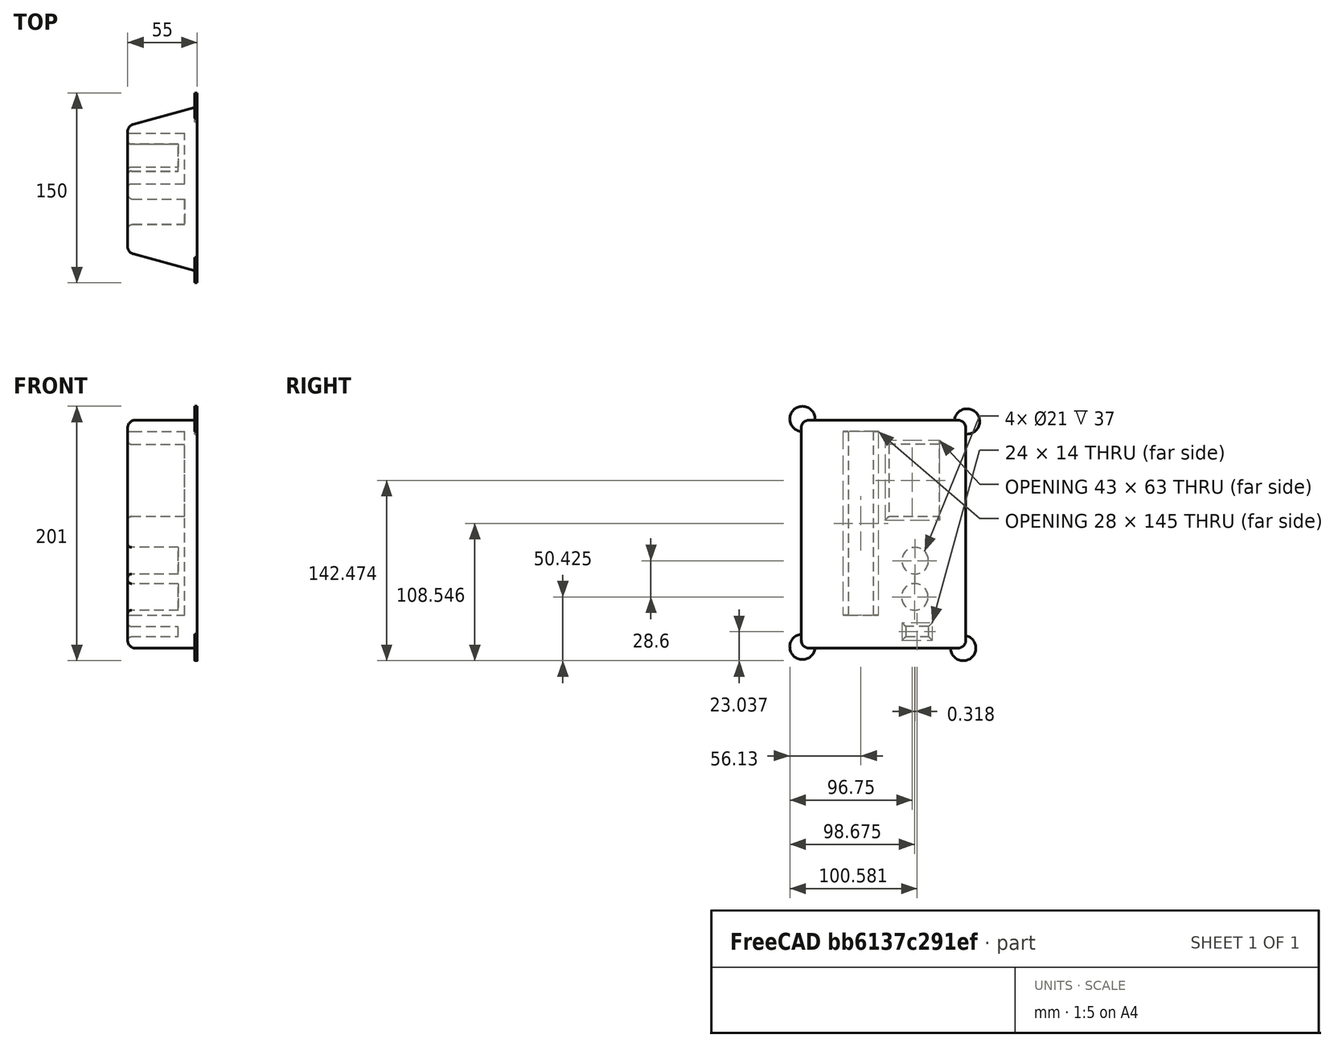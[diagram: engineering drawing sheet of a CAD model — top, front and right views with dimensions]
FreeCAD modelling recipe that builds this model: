
FCSTD DOCUMENT  (FreeCAD 0.19R)
Label: KeyboardTray
License: All rights reserved
LicenseURL: http://en.wikipedia.org/wiki/All_rights_reserved
objects: PartDesign::Fillet×5, Sketcher::SketchObject×4, Part::Cylinder×4, PartDesign::Pocket×3, PartDesign::Pad×1, PartDesign::Body×1, Part::MultiFuse×1, Mesh::Feature×1
note: 28 computed .brp shape members not serialized (recipe doc carries the construction recipe); baked Part::Feature solids carry a one-line shape summary decoded from their .brp

FEATURE [Sketcher::SketchObject] Sketch
  FullyConstrained = true
  MapMode = 5
  Support = -> [XY_Plane]
  sketch-geometry (4):
    g0: LineSegment StartX=-55 StartY=50 StartZ=0 EndX=0 EndY=65 EndZ=0
    g1: LineSegment StartX=0 StartY=65 StartZ=0 EndX=0 EndY=-65 EndZ=0
    g2: LineSegment StartX=0 StartY=-65 StartZ=0 EndX=-55 EndY=-50 EndZ=0
    g3: LineSegment StartX=-55 StartY=-50 StartZ=0 EndX=-55 EndY=50 EndZ=0
  constraints (10):
    c: Coincident(g0,g1)
    c: Coincident(g1,g2)
    c: Coincident(g2,g3)
    c: Coincident(g3,g0)
    c: Distance(g1) = 130
    c: Distance(g3) = 100
    c: DistanceX(g0,g0) = 55
    c: PointOnObject(g1,g-2)
    c: Symmetric(g1,g0,g-1)
    c: Symmetric(g2,g0,g-1)
FEATURE [PartDesign::Pad] Pad
  Direction = (1,1,1)
  Length = 180
  Length2 = 100
  Midplane = true
  Profile = -> Sketch
  Type = 0
FEATURE [Sketcher::SketchObject] Sketch001
  FullyConstrained = false
  MapMode = 5
  Placement = pos=(-55,0,0) rot=(0.57735,-0.57735,-0.57735;2.0944rad)
  Support = -> [Pad]
  sketch-geometry (4):
    g0: LineSegment StartX=7.87036 StartY=81.0461 StartZ=0 EndX=27.8704 EndY=81.0461 EndZ=0
    g1: LineSegment StartX=27.8704 StartY=81.0461 StartZ=0 EndX=27.7064 EndY=-63.9538 EndZ=0
    g2: LineSegment StartX=27.7064 StartY=-63.9538 StartZ=0 EndX=7.87036 EndY=-63.9538 EndZ=0
    g3: LineSegment StartX=7.87036 StartY=-63.9538 StartZ=0 EndX=7.87036 EndY=81.0461 EndZ=0
  constraints (9):
    c: Coincident(g0,g1)
    c: Coincident(g1,g2)
    c: Coincident(g2,g3)
    c: Coincident(g3,g0)
    c: Horizontal(g2)
    c: Vertical(g3)
    c: Distance(g1) = 145
    c: Distance(g0) = 20
    c: Perpendicular(g0,g3)
FEATURE [PartDesign::Pocket] Pocket
  BaseFeature = -> Pad
  Length = 45
  Length2 = 100
  Profile = -> Sketch001
  Type = 0
FEATURE [Sketcher::SketchObject] Sketch002
  FullyConstrained = false
  MapMode = 5
  Placement = pos=(-55,0,0) rot=(0.57735,-0.57735,-0.57735;2.0944rad)
  Support = -> [Pocket]
  sketch-geometry (4):
    g0: LineSegment StartX=-44.2497 StartY=70.9741 StartZ=0 EndX=-4.24974 EndY=70.9741 EndZ=0
    g1: LineSegment StartX=-4.24974 StartY=70.9741 StartZ=0 EndX=-4.24974 EndY=13.9741 EndZ=0
    g2: LineSegment StartX=-4.24974 StartY=13.9741 StartZ=0 EndX=-44.2497 EndY=13.9741 EndZ=0
    g3: LineSegment StartX=-44.2497 StartY=13.9741 StartZ=0 EndX=-44.2497 EndY=70.9741 EndZ=0
  constraints (10):
    c: Coincident(g0,g1)
    c: Coincident(g1,g2)
    c: Coincident(g2,g3)
    c: Coincident(g3,g0)
    c: Horizontal(g0)
    c: Horizontal(g2)
    c: Vertical(g1)
    c: Vertical(g3)
    c: Distance(g3) = 57
    c: Distance(g0) = 40
FEATURE [PartDesign::Pocket] Pocket001
  BaseFeature = -> Pocket
  Length = 45
  Length2 = 100
  Profile = -> Sketch002
  Type = 0
FEATURE [Sketcher::SketchObject] Sketch003
  FullyConstrained = false
  MapMode = 5
  Placement = pos=(-55,0,0) rot=(0.57735,-0.57735,-0.57735;2.0944rad)
  Support = -> [Pocket001]
  sketch-geometry (6):
    g0: Circle CenterX=-24.9923 CenterY=-20.9749 CenterZ=0 NormalX=0 NormalY=0 NormalZ=1 AngleXU=0 Radius=10.5
    g1: Circle CenterX=-24.6747 CenterY=-49.5749 CenterZ=0 NormalX=0 NormalY=0 NormalZ=1 AngleXU=0 Radius=10.5
    g2: LineSegment StartX=-35.5813 StartY=-72.9626 StartZ=0 EndX=-17.5813 EndY=-72.9626 EndZ=0
    g3: LineSegment StartX=-17.5813 StartY=-72.9626 StartZ=0 EndX=-17.5813 EndY=-80.9626 EndZ=0
    g4: LineSegment StartX=-17.5813 StartY=-80.9626 StartZ=0 EndX=-35.5813 EndY=-80.9626 EndZ=0
    g5: LineSegment StartX=-35.5813 StartY=-80.9626 StartZ=0 EndX=-35.5813 EndY=-72.9626 EndZ=0
  constraints (12):
    c: Radius(g1) = 10.5
    c: Equal(g1,g0)
    c: Coincident(g2,g3)
    c: Coincident(g3,g4)
    c: Coincident(g4,g5)
    c: Coincident(g5,g2)
    c: Horizontal(g2)
    c: Horizontal(g4)
    c: Vertical(g3)
    c: Vertical(g5)
    c: Distance(g2) = 18
    c: Distance(g3) = 8
FEATURE [PartDesign::Pocket] Pocket002
  BaseFeature = -> Pocket001
  Length = 40
  Length2 = 100
  Profile = -> Sketch003
  Type = 0
FEATURE [Part::Cylinder] Cylinder002
  Angle = 360
  AttacherType = Attacher::AttachEngine3D
  Height = 2
  Placement = pos=(-2,-64,-89) rot=(0,1,0;1.5708rad)
  Radius = 10
FEATURE [Part::Cylinder] Cylinder003
  Angle = 360
  AttacherType = Attacher::AttachEngine3D
  Height = 2
  Placement = pos=(-2,63,-90) rot=(0,1,0;1.5708rad)
  Radius = 10
FEATURE [Part::Cylinder] Cylinder001
  Angle = 360
  AttacherType = Attacher::AttachEngine3D
  Height = 2
  Placement = pos=(-2,-64,91) rot=(0,1,0;1.5708rad)
  Radius = 10
FEATURE [Part::Cylinder] Cylinder
  Angle = 360
  AttacherType = Attacher::AttachEngine3D
  Height = 2
  Placement = pos=(-2,66,89) rot=(0,1,0;1.5708rad)
  Radius = 10
FEATURE [PartDesign::Fillet] Fillet
  Base = -> Pocket002 [Edge25,Edge3,Edge1,Edge5,Edge6,Edge7,Edge26,Edge4]
  BaseFeature = -> Pocket002
  Radius = 6
  SupportTransform = false
FEATURE [PartDesign::Fillet] Fillet001
  Base = -> Fillet [Edge43,Edge44]
  BaseFeature = -> Fillet
  Radius = 3
  SupportTransform = false
FEATURE [PartDesign::Fillet] Fillet002
  Base = -> Fillet001 [Edge9,Edge6]
  BaseFeature = -> Fillet001
  Radius = 4
  SupportTransform = false
FEATURE [PartDesign::Fillet] Fillet003
  Base = -> Fillet002 [Edge17,Edge16,Edge15]
  BaseFeature = -> Fillet002
  Radius = 3
  SupportTransform = false
FEATURE [PartDesign::Fillet] Fillet004
  Base = -> Fillet003 [Edge23,Edge20,Edge22,Edge21]
  BaseFeature = -> Fillet003
  Radius = 3
  SupportTransform = false
FEATURE [PartDesign::Body] Body
  Group = -> [Sketch,Pad,Sketch001,Pocket,Sketch002,Pocket001,Sketch003,Pocket002,Fillet,Fillet001,Fillet002,Fillet003,Fillet004]
  Origin = -> Origin
  Tip = -> Fillet004
FEATURE [Part::MultiFuse] Fusion
  Shapes = -> [Fillet004,Cylinder,Cylinder001,Cylinder002,Cylinder003]
FEATURE [Mesh::Feature] Mesh  label="Fusion (Meshed)"
